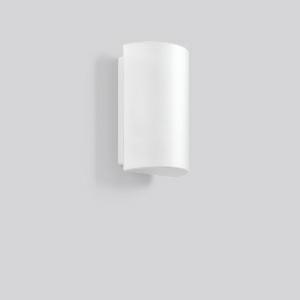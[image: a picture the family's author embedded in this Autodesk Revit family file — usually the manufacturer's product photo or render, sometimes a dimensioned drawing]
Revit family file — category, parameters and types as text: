
# Revit family: colonna_ip_44_211423_002_c755
name_source: partatom
category: Lighting Fixtures
units: mm (PartAtom-declared; Revit-internal decimal feet)

## family parameters
Cut with Voids When Loaded = No
Host = Face
Light Source = No
Part Type = Normal
Room Calculation Point = No
Round Connector Dimension = Use Diameter
Shared = No

## types (1)
- COLONNA IP 44 (1 x LED Modul 830, 900 lm, 3000)
    Apparent Load = 9 VA
    CIE Flux Codes = 27 53 77 50 100
    Color Rendering = 80
    Color Temperature = 3000
    Default Elevation = 1800 mm
    Description = Series: COLONNA IP 44
Classic wall luminaire with semicircular glass. Base: plastic. Opal glass: mouth-blown, satin finish. Diffuser fastening: spring system. 
Colour: white
Length: 245 mm
Width: 145 mm
Height: 110 mm
Lamp: LED
Socket: without socket
Colour temperature: 3000K
Colour rendering index (CRI): 80
System power: 9 W
Rated luminous flux: 900 lm
Luminous efficiency: 100 lm/W
Control gear: Regulated power supply
Protection class: I
Type of protection: IP 44
    Height = 110 mm
    Lamp = 1 x LED Modul 830
    Lamp Light Flux = 900 lm
    Lamp count = 1
    Length = 245 mm
    Lifetime = 50000 h
    Luminous efficacy = 100 lm/W
    Manufacturer = RZB
    ModVariant = No
    Model = 211423.002
    Mounting Place = Wall
    Mounting Type = Surface mounted
    Number of Poles = 1
    OnlyDefault = Yes
    Power Factor = 1
    Product Name = COLONNA IP 44
    Product group = Surface mounted Wall luminaires
    ProductGroupID = 2001
    Protection Class = Protection class I
    Protection Degree = IP 44
    RLX_Detail_Level = 1
    RLX_Emergency_Light_Flux = 0 lm
    RLX_Emergency_Type = 0
    RLX_Emergency_Type_DB = No
    RlxData = <blob elided: 37581 chars, md5=41841ee9>
    Socket = socket
    Standby Power = 0 W
    System Light Flux = 900 lm
    System Power = 9 W
    Type Comments = Product without accessories
    Type Image = 211324.002.jpg
    URL = http://relux.com
    VarID = ---
    Voltage = 230 V
    Voltage Range = 220-240 V
    Weight = 0.00 kg
    Width = 145 mm

## geometry (parser evidence)
native form markers: Blend x4, Sweep x12
no freeform markers — native parametric forms only
